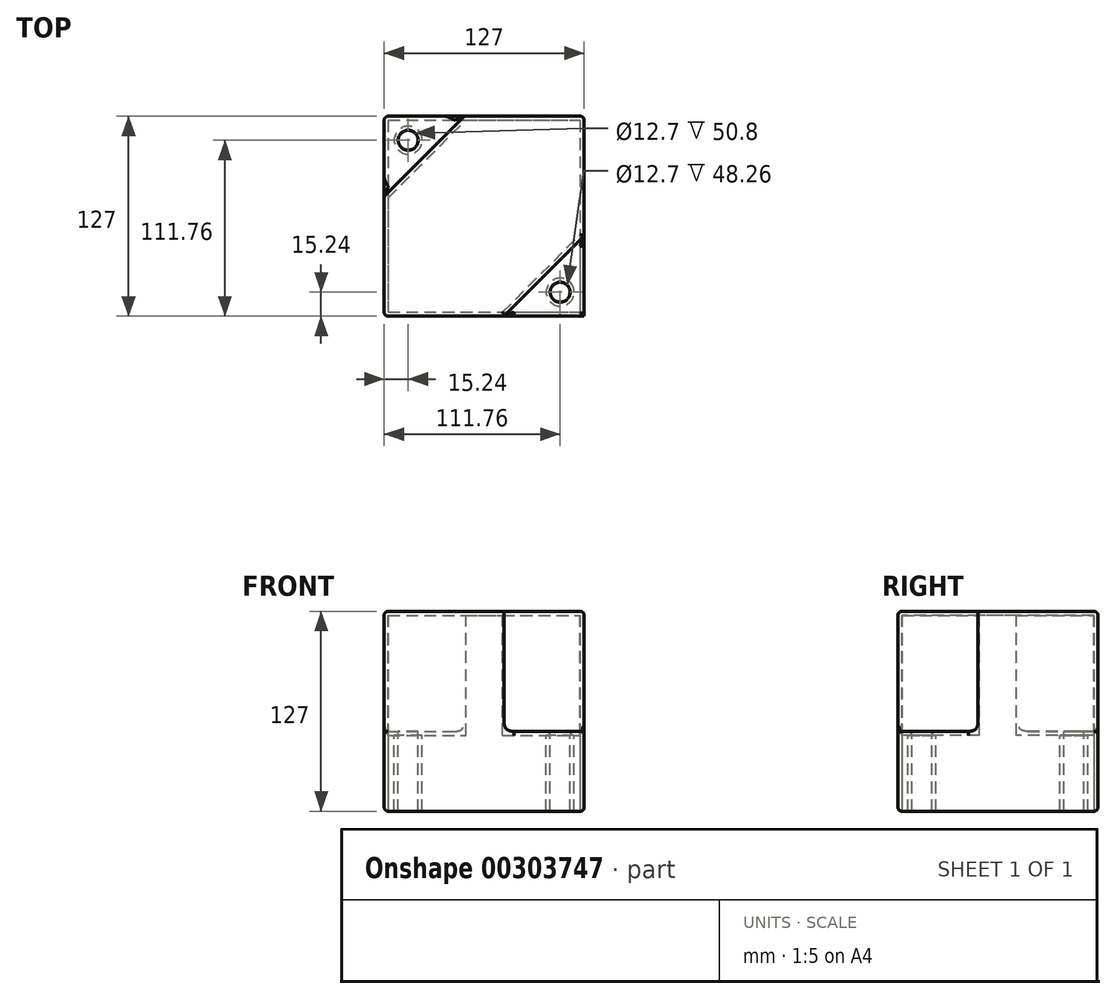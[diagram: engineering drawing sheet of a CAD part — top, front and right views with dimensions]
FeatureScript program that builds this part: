
annotation { "Feature Type Name" : "Feature", "Feature Type Description" : "" }
export const myFeature = defineFeature(function(context is Context, id is Id, definition is map)
    precondition{}
    {
        {
            var Q0;
            Q0=qCreatedBy(makeId("Top.planeOp"),FACE);
            var sketch = newSketch(context, id + "F0", { "sketchPlane" : qUnion([Q0])});
            skLineSegment(sketch, "E0.bottom", {"start": v(-63.5, 63.5) * mm, "end": v(63.5, 63.5) * mm});
            skLineSegment(sketch, "E0.top", {"start": v(-63.5, -63.5) * mm, "end": v(63.5, -63.5) * mm});
            skLineSegment(sketch, "E0.left", {"start": v(-63.5, 63.5) * mm, "end": v(-63.5, -63.5) * mm});
            skLineSegment(sketch, "E0.right", {"start": v(63.5, 63.5) * mm, "end": v(63.5, -63.5) * mm});
            skPoint(sketch, "E0.middle", {"position": v(0, 0) * mm});
            skSolve(sketch);
        }
        {
            var Q0;
            Q0=makeQuery(id+"F0.imprint","IMPRINT",FACE,{"disambiguationData":[TD([[makeQuery(id+"F0.imprint","IMPRINT",EDGE,{"derivedFrom":sQuery(id+"F0.wireOp",EDGE,"E0.bottom")}),-1.0]])]});
            extrude(context, id + "F1", {"entities" : qUnion([Q0]), "endBound" : BoundingType.SYMMETRIC, "depth" : 127 * mm});
        }
        {
            var Q0;
            Q0=makeQuery(id+"F1.opExtrude","CAP_FACE",FACE,{"disambiguationData":[OSD([sQuery(id+"F0.wireOp",EDGE,"E0.bottom"),sQuery(id+"F0.wireOp",EDGE,"E0.top"),sQuery(id+"F0.wireOp",EDGE,"E0.left"),sQuery(id+"F0.wireOp",EDGE,"E0.right")])],"isStart":false});
            var sketch = newSketch(context, id + "F2", { "sketchPlane" : qUnion([Q0])});
            skLineSegment(sketch, "E1", {"start": v(-63.5, 63.5) * mm, "end": v(-63.5, 12.7) * mm, "construction": true});
            skLineSegment(sketch, "E2", {"start": v(-63.5, 12.7) * mm, "end": v(-12.7, 63.5) * mm, "construction": true});
            skLineSegment(sketch, "E3", {"start": v(-12.7, 63.5) * mm, "end": v(-63.5, 63.5) * mm, "construction": true});
            skLineSegment(sketch, "E4", {"start": v(63.5, -63.5) * mm, "end": v(12.7, -63.5) * mm, "construction": true});
            skLineSegment(sketch, "E5", {"start": v(12.7, -63.5) * mm, "end": v(63.5, -12.7) * mm, "construction": true});
            skLineSegment(sketch, "E6", {"start": v(63.5, -12.7) * mm, "end": v(63.5, -63.5) * mm, "construction": true});
            skLineSegment(sketch, "E7", {"start": v(-63.5, -63.5) * mm, "end": v(0, 0) * mm, "construction": true});
            skLineSegment(sketch, "E8", {"start": v(0, 0) * mm, "end": v(63.5, 63.5) * mm, "construction": true});
            skLineSegment(sketch, "E9", {"start": v(-63.5, 12.7) * mm, "end": v(-12.7, 63.5) * mm});
            skLineSegment(sketch, "E10", {"start": v(-63.5, 63.5) * mm, "end": v(-63.5, 12.7) * mm});
            skLineSegment(sketch, "E11", {"start": v(12.7, -63.5) * mm, "end": v(63.5, -12.7) * mm});
            skLineSegment(sketch, "E12", {"start": v(63.5, -63.5) * mm, "end": v(12.7, -63.5) * mm});
            skSolve(sketch);
        }
        {
            var Q0;
            {var subQ0=sQuery(id+"F2.wireOp",EDGE,"E9");Q0=makeQuery(id+"F2.imprint","IMPRINT",FACE,{"disambiguationData":[TD([[makeQuery(id+"F2.imprint","IMPRINT",EDGE,{"derivedFrom":subQ0}),1.0]])]});}
            var Q1;
            {var subQ0=sQuery(id+"F2.wireOp",EDGE,"E11");Q1=makeQuery(id+"F2.imprint","IMPRINT",FACE,{"disambiguationData":[TD([[makeQuery(id+"F2.imprint","IMPRINT",EDGE,{"derivedFrom":subQ0}),-1.0]])]});}
            extrude(context, id + "F3", {"entities" : qUnion([Q0, Q1]), "operationType" : NewBodyOperationType.REMOVE, "oppositeDirection" : true, "depth" : 76.2 * mm});
        }
        {
            var Q0;
            Q0=qCreatedBy(makeId("Top.planeOp"),FACE);
            var sketch = newSketch(context, id + "F4", { "sketchPlane" : qUnion([Q0])});
            skCircle(sketch, "E13", {"center": v(-48.26, 48.26) * mm, "radius": 6.35 * mm});
            skCircle(sketch, "E14", {"center": v(48.26, -48.26) * mm, "radius": 6.35 * mm});
            skSolve(sketch);
        }
        {
            var Q0;
            Q0=makeQuery(id+"F4.imprint","IMPRINT",FACE,{"disambiguationData":[TD([[makeQuery(id+"F4.imprint","IMPRINT",EDGE,{"derivedFrom":sQuery(id+"F4.wireOp",EDGE,"E14")}),1.0]])]});
            var Q1;
            Q1=makeQuery(id+"F4.imprint","IMPRINT",FACE,{"disambiguationData":[TD([[makeQuery(id+"F4.imprint","IMPRINT",EDGE,{"derivedFrom":sQuery(id+"F4.wireOp",EDGE,"E13")}),1.0]])]});
            extrude(context, id + "F5", {"entities" : qUnion([Q0, Q1]), "operationType" : NewBodyOperationType.REMOVE, "oppositeDirection" : true, "depth" : 203.2 * mm});
        }
        {
            var Q0;
            Q0=makeQuery(id+"F1.opExtrude","CAP_FACE",FACE,{"disambiguationData":[OSD([sQuery(id+"F0.wireOp",EDGE,"E0.bottom"),sQuery(id+"F0.wireOp",EDGE,"E0.top"),sQuery(id+"F0.wireOp",EDGE,"E0.left"),sQuery(id+"F0.wireOp",EDGE,"E0.right")])],"isStart":true});
            shell(context, id + "F6", {"entities" : qUnion([Q0]), "thickness" : 2.54 * mm});
        }
        {
            var Q0;
            Q0=makeQuery(id+"F1.opExtrude","CAP_EDGE",EDGE,{"disambiguationData":[OSD([sQuery(id+"F0.wireOp",EDGE,"E0.top")])],"isStart":false});
            var Q1;
            Q1=makeQuery(id+"F1.opExtrude","CAP_FACE",FACE,{"disambiguationData":[OSD([sQuery(id+"F0.wireOp",EDGE,"E0.bottom"),sQuery(id+"F0.wireOp",EDGE,"E0.top"),sQuery(id+"F0.wireOp",EDGE,"E0.left"),sQuery(id+"F0.wireOp",EDGE,"E0.right")])],"isStart":false});
            var Q2;
            Q2=makeQuery(id+"F1.opExtrude","SWEPT_EDGE",EDGE,{"disambiguationData":[OSD([sQuery(id+"F0.wireOp",EDGE,"E0.bottom"),sQuery(id+"F0.wireOp",EDGE,"E0.right")])]});
            var Q3;
            Q3=makeQuery(id+"F3.boolean.opBoolean","COPY",EDGE,{"derivedFrom":makeQuery(id+"F3.opExtrude","SWEPT_EDGE",EDGE,{"disambiguationData":[OSD([sQuery(id+"F0.wireOp",EDGE,"E0.right"),sQuery(id+"F2.wireOp",EDGE,"E11")])]})});
            var Q4;
            Q4=makeQuery(id+"F3.boolean.opBoolean","COPY",EDGE,{"derivedFrom":makeQuery(id+"F3.opExtrude","SWEPT_EDGE",EDGE,{"disambiguationData":[OSD([sQuery(id+"F0.wireOp",EDGE,"E0.top"),sQuery(id+"F2.wireOp",EDGE,"E11"),sQuery(id+"F2.wireOp",EDGE,"E12")])]})});
            var Q5;
            Q5=makeQuery(id+"F3.boolean.opBoolean","COPY",EDGE,{"derivedFrom":makeQuery(id+"F3.opExtrude","CAP_EDGE",EDGE,{"disambiguationData":[OSD([sQuery(id+"F2.wireOp",EDGE,"E12")])],"isStart":false})});
            var Q6;
            Q6=makeQuery(id+"F3.boolean.opBoolean","COPY",EDGE,{"derivedFrom":makeQuery(id+"F3.opExtrude","CAP_EDGE",EDGE,{"disambiguationData":[OSD([sQuery(id+"F2.wireOp",EDGE,"E11")])],"isStart":false})});
            var Q7;
            Q7=makeQuery(id+"F3.boolean.opBoolean","COPY",FACE,{"derivedFrom":makeQuery(id+"F3.opExtrude","CAP_FACE",FACE,{"disambiguationData":[OSD([sQuery(id+"F0.wireOp",EDGE,"E0.right"),sQuery(id+"F2.wireOp",EDGE,"E11"),sQuery(id+"F2.wireOp",EDGE,"E12")])],"isStart":false})});
            var Q8;
            Q8=makeQuery(id+"F1.opExtrude","CAP_EDGE",EDGE,{"disambiguationData":[OSD([sQuery(id+"F0.wireOp",EDGE,"E0.top")])],"isStart":true});
            var Q9;
            Q9=makeQuery(id+"F1.opExtrude","CAP_EDGE",EDGE,{"disambiguationData":[OSD([sQuery(id+"F0.wireOp",EDGE,"E0.right")])],"isStart":true});
            var Q10;
            Q10=makeQuery(id+"F3.boolean.opBoolean","COPY",FACE,{"derivedFrom":makeQuery(id+"F3.opExtrude","SWEPT_FACE",FACE,{"disambiguationData":[OSD([sQuery(id+"F2.wireOp",EDGE,"E9")])]})});
            var Q11;
            Q11=makeQuery(id+"F3.boolean.opBoolean","COPY",EDGE,{"derivedFrom":makeQuery(id+"F3.opExtrude","CAP_EDGE",EDGE,{"disambiguationData":[OSD([sQuery(id+"F2.wireOp",EDGE,"E10")])],"isStart":false})});
            var Q12;
            Q12=makeQuery(id+"F3.boolean.opBoolean","COPY",EDGE,{"derivedFrom":makeQuery(id+"F3.opExtrude","CAP_EDGE",EDGE,{"disambiguationData":[OSD([sQuery(id+"F0.wireOp",EDGE,"E0.bottom")])],"isStart":false})});
            var Q13;
            Q13=makeQuery(id+"F1.opExtrude","SWEPT_EDGE",EDGE,{"disambiguationData":[OSD([sQuery(id+"F0.wireOp",EDGE,"E0.bottom"),sQuery(id+"F0.wireOp",EDGE,"E0.left")])]});
            var Q14;
            Q14=makeQuery(id+"F1.opExtrude","CAP_EDGE",EDGE,{"disambiguationData":[OSD([sQuery(id+"F0.wireOp",EDGE,"E0.left")])],"isStart":true});
            var Q15;
            Q15=makeQuery(id+"F1.opExtrude","CAP_EDGE",EDGE,{"disambiguationData":[OSD([sQuery(id+"F0.wireOp",EDGE,"E0.bottom")])],"isStart":true});
            var Q16;
            Q16=makeQuery(id+"F1.opExtrude","SWEPT_EDGE",EDGE,{"disambiguationData":[OSD([sQuery(id+"F0.wireOp",EDGE,"E0.top"),sQuery(id+"F0.wireOp",EDGE,"E0.left")])]});
            fillet(context, id + "F7", {"entities" : qUnion([Q0, Q1, Q2, Q3, Q4, Q5, Q6, Q7, Q8, Q9, Q10, Q11, Q12, Q13, Q14, Q15, Q16]), "radius" : 2.54 * mm, "tangentPropagation" : true, "allowEdgeOverflow" : false});
        }
    });
